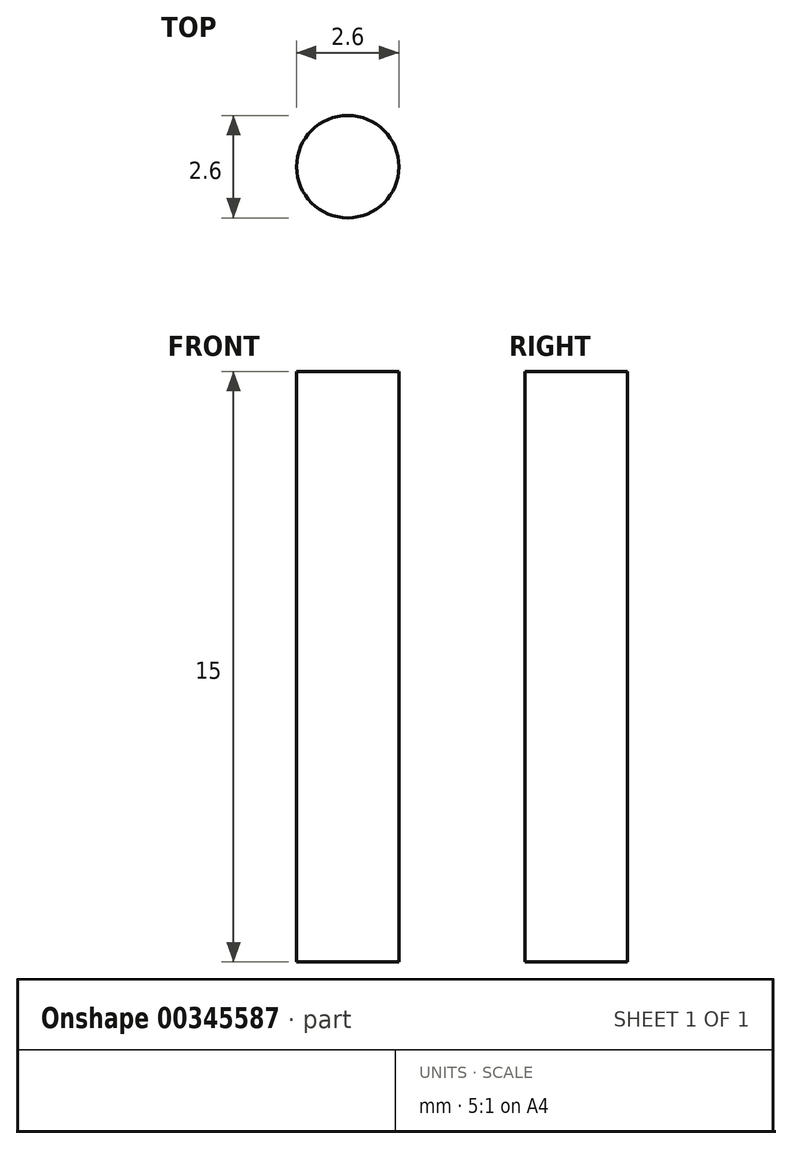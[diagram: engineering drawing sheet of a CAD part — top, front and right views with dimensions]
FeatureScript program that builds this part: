
annotation { "Feature Type Name" : "Feature", "Feature Type Description" : "" }
export const myFeature = defineFeature(function(context is Context, id is Id, definition is map)
    precondition{}
    {
        {
            var Q0;
            Q0=qCreatedBy(makeId("Top.planeOp"),FACE);
            var sketch = newSketch(context, id + "F0", { "sketchPlane" : qUnion([Q0])});
            skCircle(sketch, "E0", {"center": v(-27.35, 30.37) * mm, "radius": 1.3 * mm});
            skSolve(sketch);
        }
        {
            var Q0;
            Q0 = qSketchRegion(id + "F0", true);
            extrude(context, id + "F1", {"entities" : qUnion([Q0]), "depth" : 15 * mm});
        }
    });
